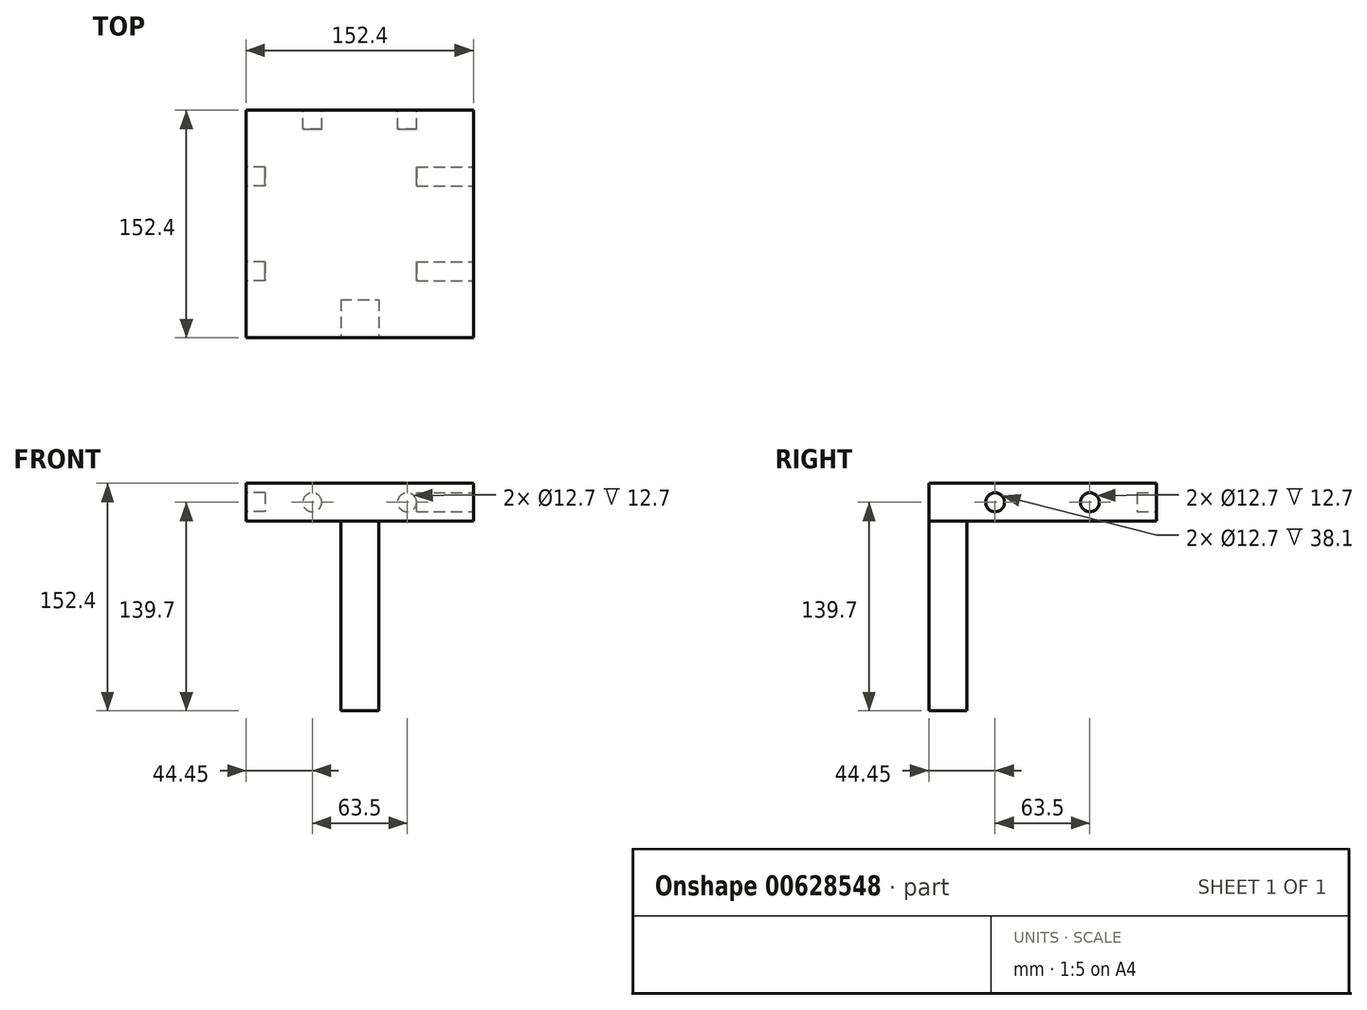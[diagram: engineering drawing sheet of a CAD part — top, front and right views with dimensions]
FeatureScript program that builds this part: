
annotation { "Feature Type Name" : "Feature", "Feature Type Description" : "" }
export const myFeature = defineFeature(function(context is Context, id is Id, definition is map)
    precondition{}
    {
        {
            var Q0;
            Q0=qCreatedBy(makeId("Front.planeOp"),FACE);
            var sketch = newSketch(context, id + "F0", { "sketchPlane" : qUnion([Q0])});
            skLineSegment(sketch, "E0.bottom", {"start": v(0, 0) * mm, "end": v(0, 0) * mm});
            skLineSegment(sketch, "E0.top", {"start": v(0, 0) * mm, "end": v(0, 0) * mm});
            skLineSegment(sketch, "E0.left", {"start": v(0, 0) * mm, "end": v(0, 0) * mm});
            skLineSegment(sketch, "E0.right", {"start": v(0, 0) * mm, "end": v(0, 0) * mm});
            skPoint(sketch, "E0.middle", {"position": v(0, 0) * mm});
            skLineSegment(sketch, "E1.bottom", {"start": v(-12.7, 76.2) * mm, "end": v(12.7, 76.2) * mm});
            skLineSegment(sketch, "E1.top", {"start": v(-12.7, -76.2) * mm, "end": v(12.7, -76.2) * mm});
            skLineSegment(sketch, "E1.left", {"start": v(-12.7, 50.8) * mm, "end": v(-12.7, -76.2) * mm});
            skLineSegment(sketch, "E1.right", {"start": v(12.7, 50.8) * mm, "end": v(12.7, -76.2) * mm});
            skLineSegment(sketch, "E2.bottom", {"start": v(-76.2, 76.2) * mm, "end": v(76.2, 76.2) * mm});
            skLineSegment(sketch, "E2.top", {"start": v(-76.2, 50.8) * mm, "end": v(76.2, 50.8) * mm});
            skLineSegment(sketch, "E2.left", {"start": v(-76.2, 76.2) * mm, "end": v(-76.2, 50.8) * mm});
            skLineSegment(sketch, "E2.right", {"start": v(76.2, 76.2) * mm, "end": v(76.2, 50.8) * mm});
            skSolve(sketch);
        }
        {
            var Q0;
            {var subQ4=sQuery(id+"F0.wireOp",EDGE,"E2.left");Q0=makeQuery(id+"F0.imprint","IMPRINT",FACE,{"disambiguationData":[TD([[makeQuery(id+"F0.imprint","IMPRINT",EDGE,{"derivedFrom":subQ4}),1.0]])]});}
            extrude(context, id + "F1", {"entities" : qUnion([Q0]), "oppositeDirection" : true, "depth" : 152.4 * mm, "offsetDistance" : 25.4 * mm});
        }
        {
            var Q0;
            Q0=makeQuery(id+"F0.imprint","IMPRINT",FACE,{"disambiguationData":[TD([[makeQuery(id+"F0.imprint","IMPRINT",EDGE,{"derivedFrom":sQuery(id+"F0.wireOp",EDGE,"E1.top")}),1.0]])]});
            extrude(context, id + "F2", {"entities" : qUnion([Q0]), "oppositeDirection" : true, "depth" : 25.4 * mm, "offsetDistance" : 25.4 * mm});
        }
        {
            var Q0;
            Q0=makeQuery(id+"F1.opExtrude","SWEPT_FACE",FACE,{"disambiguationData":[OSD([sQuery(id+"F0.wireOp",EDGE,"E2.left")])]});
            var sketch = newSketch(context, id + "F3", { "sketchPlane" : qUnion([Q0])});
            skCircle(sketch, "E3", {"center": v(-107.95, 63.5) * mm, "radius": 6.35 * mm});
            skPoint(sketch, "E3.centerSnap0", {"position": v(-152.4, 63.5) * mm});
            skCircle(sketch, "E4", {"center": v(-44.45, 63.5) * mm, "radius": 6.35 * mm});
            skSolve(sketch);
        }
        {
            var Q0;
            Q0=makeQuery(id+"F3.imprint","IMPRINT",FACE,{"disambiguationData":[TD([[makeQuery(id+"F3.imprint","IMPRINT",EDGE,{"derivedFrom":sQuery(id+"F3.wireOp",EDGE,"E3")}),1.0]])]});
            var Q1;
            Q1=makeQuery(id+"F3.imprint","IMPRINT",FACE,{"disambiguationData":[TD([[makeQuery(id+"F3.imprint","IMPRINT",EDGE,{"derivedFrom":sQuery(id+"F3.wireOp",EDGE,"E4")}),1.0]])]});
            var Q2;
            Q2=sQuery(id+"F3.wireOp",EDGE,"E3");
            extrude(context, id + "F4", {"entities" : qUnion([Q0, Q1]), "operationType" : NewBodyOperationType.REMOVE, "surfaceEntities" : qUnion([Q2]), "oppositeDirection" : true, "depth" : 12.7 * mm, "offsetDistance" : 25.4 * mm});
        }
        {
            var Q0;
            Q0=makeQuery(id+"F1.opExtrude","CAP_FACE",FACE,{"disambiguationData":[OSD([sQuery(id+"F0.wireOp",EDGE,"E2.bottom"),sQuery(id+"F0.wireOp",EDGE,"E2.top"),sQuery(id+"F0.wireOp",EDGE,"E2.left"),sQuery(id+"F0.wireOp",EDGE,"E2.right")])],"isStart":false});
            var sketch = newSketch(context, id + "F5", { "sketchPlane" : qUnion([Q0])});
            skCircle(sketch, "E5", {"center": v(-31.75, 63.5) * mm, "radius": 6.35 * mm});
            skPoint(sketch, "E5.centerSnap0", {"position": v(-76.2, 63.5) * mm});
            skCircle(sketch, "E6", {"center": v(31.75, 63.5) * mm, "radius": 6.35 * mm});
            skSolve(sketch);
        }
        {
            var Q0;
            Q0=makeQuery(id+"F5.imprint","IMPRINT",FACE,{"disambiguationData":[TD([[makeQuery(id+"F5.imprint","IMPRINT",EDGE,{"derivedFrom":sQuery(id+"F5.wireOp",EDGE,"E5")}),1.0]])]});
            var Q1;
            Q1=makeQuery(id+"F5.imprint","IMPRINT",FACE,{"disambiguationData":[TD([[makeQuery(id+"F5.imprint","IMPRINT",EDGE,{"derivedFrom":sQuery(id+"F5.wireOp",EDGE,"E6")}),1.0]])]});
            extrude(context, id + "F6", {"entities" : qUnion([Q0, Q1]), "operationType" : NewBodyOperationType.REMOVE, "oppositeDirection" : true, "depth" : 12.7 * mm, "offsetDistance" : 25.4 * mm});
        }
        {
            var Q0;
            Q0=makeQuery(id+"F1.opExtrude","SWEPT_FACE",FACE,{"disambiguationData":[OSD([sQuery(id+"F0.wireOp",EDGE,"E2.right")])]});
            var sketch = newSketch(context, id + "F7", { "sketchPlane" : qUnion([Q0])});
            skCircle(sketch, "E7", {"center": v(44.45, 63.5) * mm, "radius": 6.35 * mm});
            skPoint(sketch, "E7.centerSnap0", {"position": v(0, 63.5) * mm});
            skCircle(sketch, "E8", {"center": v(107.95, 63.5) * mm, "radius": 6.35 * mm});
            skSolve(sketch);
        }
        {
            var Q0;
            Q0=makeQuery(id+"F7.imprint","IMPRINT",FACE,{"disambiguationData":[TD([[makeQuery(id+"F7.imprint","IMPRINT",EDGE,{"derivedFrom":sQuery(id+"F7.wireOp",EDGE,"E7")}),1.0]])]});
            var Q1;
            Q1=makeQuery(id+"F7.imprint","IMPRINT",FACE,{"disambiguationData":[TD([[makeQuery(id+"F7.imprint","IMPRINT",EDGE,{"derivedFrom":sQuery(id+"F7.wireOp",EDGE,"E8")}),1.0]])]});
            extrude(context, id + "F8", {"entities" : qUnion([Q0, Q1]), "operationType" : NewBodyOperationType.REMOVE, "oppositeDirection" : true, "depth" : 38.1 * mm, "offsetDistance" : 25.4 * mm});
        }
    });
